# Revit family: Divider_Curtain-PSS-4025-Peak_Fold
name_source: partatom
category: Specialty Equipment
revit_build: Autodesk Revit 2017 (Build: 20170816_0615(x64)
units: mm (PartAtom-declared; Revit-internal decimal feet)

## family parameters
Always vertical = Yes
Cut with Voids When Loaded = No
OmniClass Number = 23.40.50.34.17
OmniClass Title = Gymnasium Dividers
Part Type = Normal
Room Calculation Point = No
Round Connector Dimension = Use Diameter
Shared = No
Work Plane-Based = No

## types (1)
- 52'-0" x 30'-0" (3 1/2_12)
    2 Hangers Required - Left = No
    2 Hangers Required - Right = No
    3 Hangers Required - Left = Yes
    3 Hangers Required - Right = Yes
    4 Hangers Required - Left = No
    4 Hangers Required - Right = No
    5 Hangers Required - Left = No
    5 Hangers Required - Right = No
    6 Hangers Required - Left = No
    6 Hangers Required - Right = No
    Assembly Code = E1020900
    BIM Version = v3.1
    Bottom of Structure Peak Height = 33' - 10"
    Bridge Pipe Requirement = If Structure exceeds 14' span
    CSI MasterFormat = 11 66 53
    Curtain Lower Material = Vinyl Coated Fabric - Performance Sports Systems - C04 Royal Blue
    Curtain Lower Material Height = 8' - 0"
    Curtain Peak Height = 30' - 0"
    Curtain Slope Angle = 16.26°
    Curtain Slope Rise per 12 = 3.5
    Curtain Upper Material = Vinyl Mesh - Performance Sports Systems - M01 White
    Description = Peak-Fold Divider Curtain
    Dim Left to First Carrier = 6"
    Dim Right to First Carrier = 6"
    Height = 30' - 0"
    Left Dim from Peak = 26' - 0"
    Length = 52' - 0"
    Manufacturer = Performance Sports Systems
    Maximum Curtain Slope = 3 1/2 : 12
    Maximum Size Limitations = 50' High (at Curtain Peak) x 120' Long
    Minimum Curtain Slope = 1/2 : 12
    Model = 4025
    Product Page URL = http://www.perfsports.com
    Right Dim from Peak = 26' - 0"
    Structure Slope Angle = 18.43°
    Structure Slope Rise per 12 = 4
    Superstructure Finish = Powder Coat - Performance Sports Systems - Black
    URL = http://www.perfsports.com

## geometry (parser evidence)
native form markers: Blend x92, Sweep x5
no freeform markers — native parametric forms only
